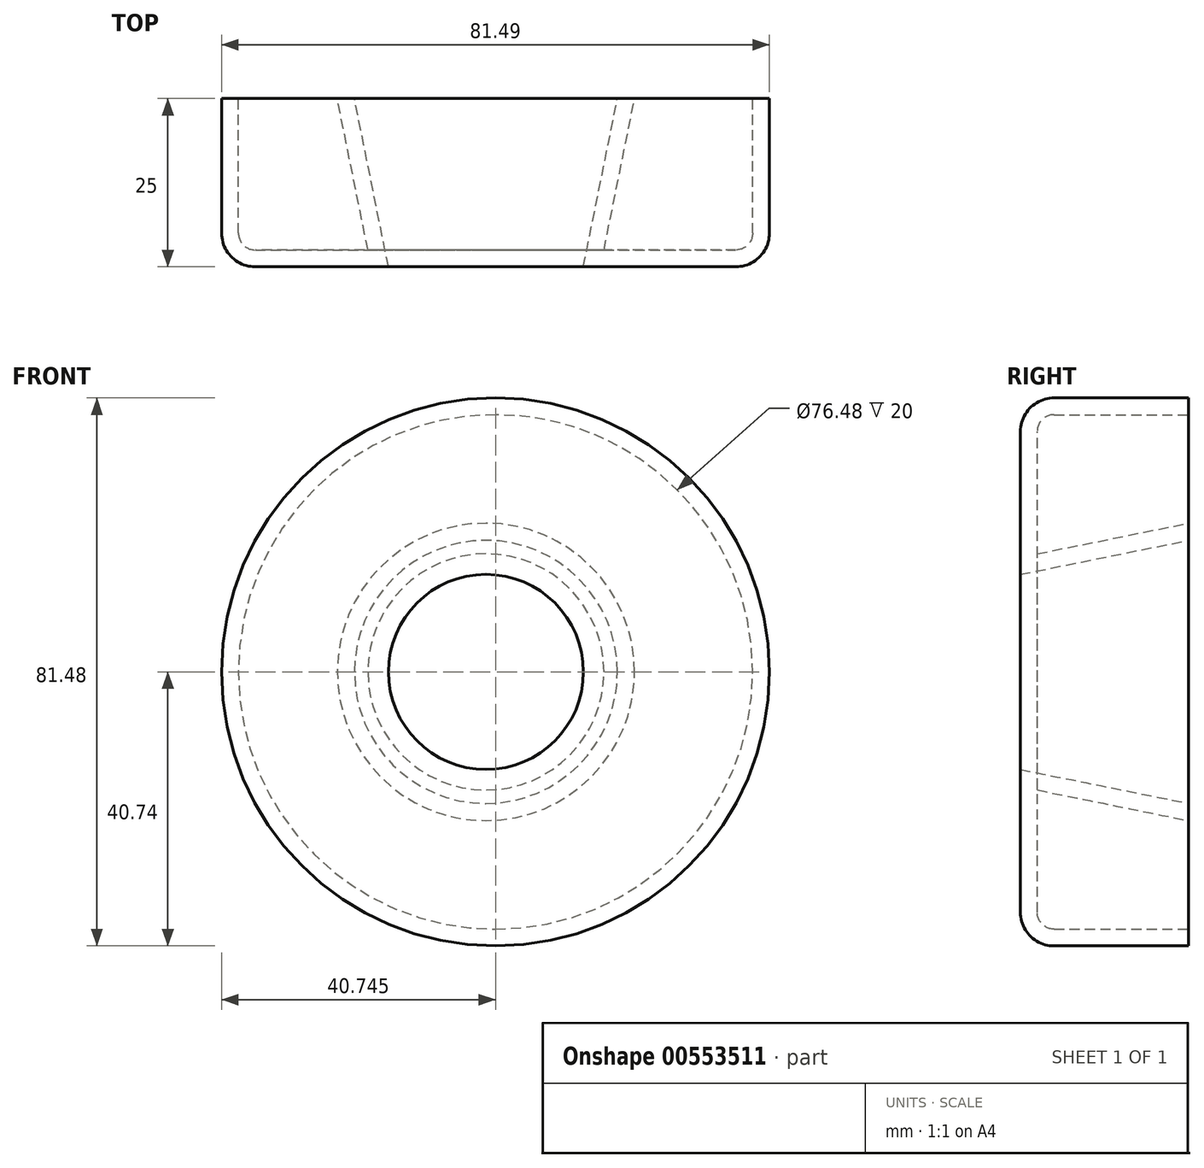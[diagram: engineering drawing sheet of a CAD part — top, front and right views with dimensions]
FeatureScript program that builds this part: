
annotation { "Feature Type Name" : "Feature", "Feature Type Description" : "" }
export const myFeature = defineFeature(function(context is Context, id is Id, definition is map)
    precondition{}
    {
        {
            var Q0;
            Q0=qCreatedBy(makeId("Front.planeOp"),FACE);
            cPlane(context, id + "F0", {"entities" : qUnion([Q0]), "cplaneType" : CPlaneType.OFFSET, "offset" : 25 * mm, "width" : 150 * mm, "height" : 150 * mm});
        }
        {
            var Q0;
            Q0=qCreatedBy(makeId("Front.planeOp"),FACE);
            var sketch = newSketch(context, id + "F1", { "sketchPlane" : qUnion([Q0])});
            skCircle(sketch, "E0", {"center": v(1.43, 0) * mm, "radius": 40.74 * mm});
            skSolve(sketch);
        }
        {
            var Q0;
            Q0 = qSketchRegion(id + "F1", true);
            extrude(context, id + "F2", {"entities" : qUnion([Q0]), "depth" : 25 * mm, "offsetDistance" : 25 * mm});
        }
        {
            var Q0;
            Q0=qCreatedBy(makeId("Front.planeOp"),FACE);
            var sketch = newSketch(context, id + "F3", { "sketchPlane" : qUnion([Q0])});
            skCircle(sketch, "E1", {"center": v(0, 0) * mm, "radius": 19.56 * mm});
            skSolve(sketch);
        }
        {
            var Q0;
            Q0=qCreatedBy(id+"F0.planeOp",FACE);
            var sketch = newSketch(context, id + "F4", { "sketchPlane" : qUnion([Q0])});
            skCircle(sketch, "E2", {"center": v(0, 0) * mm, "radius": 14.5 * mm});
            skSolve(sketch);
        }
        {
            var Q1;
            Q1 = qSketchRegion(id + "F3", true);
            var Q2;
            Q2=makeQuery(id+"F4.imprint","IMPRINT",FACE,{"disambiguationData":[TD([[makeQuery(id+"F4.imprint","IMPRINT",EDGE,{"derivedFrom":sQuery(id+"F4.wireOp",EDGE,"E2")}),1.0]])]});
            loft(context, id + "F5", {"operationType" : NewBodyOperationType.REMOVE, "sheetProfilesArray" : [{ "sheetProfileEntities" : qUnion([Q1]) }, { "sheetProfileEntities" : qUnion([Q2]) }]});
        }
        {
            var Q0;
            Q0=makeQuery(id+"F2.opExtrude","CAP_EDGE",EDGE,{"disambiguationData":[OSD([sQuery(id+"F1.wireOp",EDGE,"E0")])],"isStart":false});
            fillet(context, id + "F6", {"entities" : qUnion([Q0]), "radius" : 5 * mm, "tangentPropagation" : true, "allowEdgeOverflow" : false});
        }
        {
            var Q0;
            Q0=makeQuery(id+"F2.opExtrude","CAP_FACE",FACE,{"disambiguationData":[OSD([sQuery(id+"F1.wireOp",EDGE,"E0")])],"isStart":true});
            shell(context, id + "F7", {"entities" : qUnion([Q0]), "thickness" : 2.5 * mm});
        }
    });
